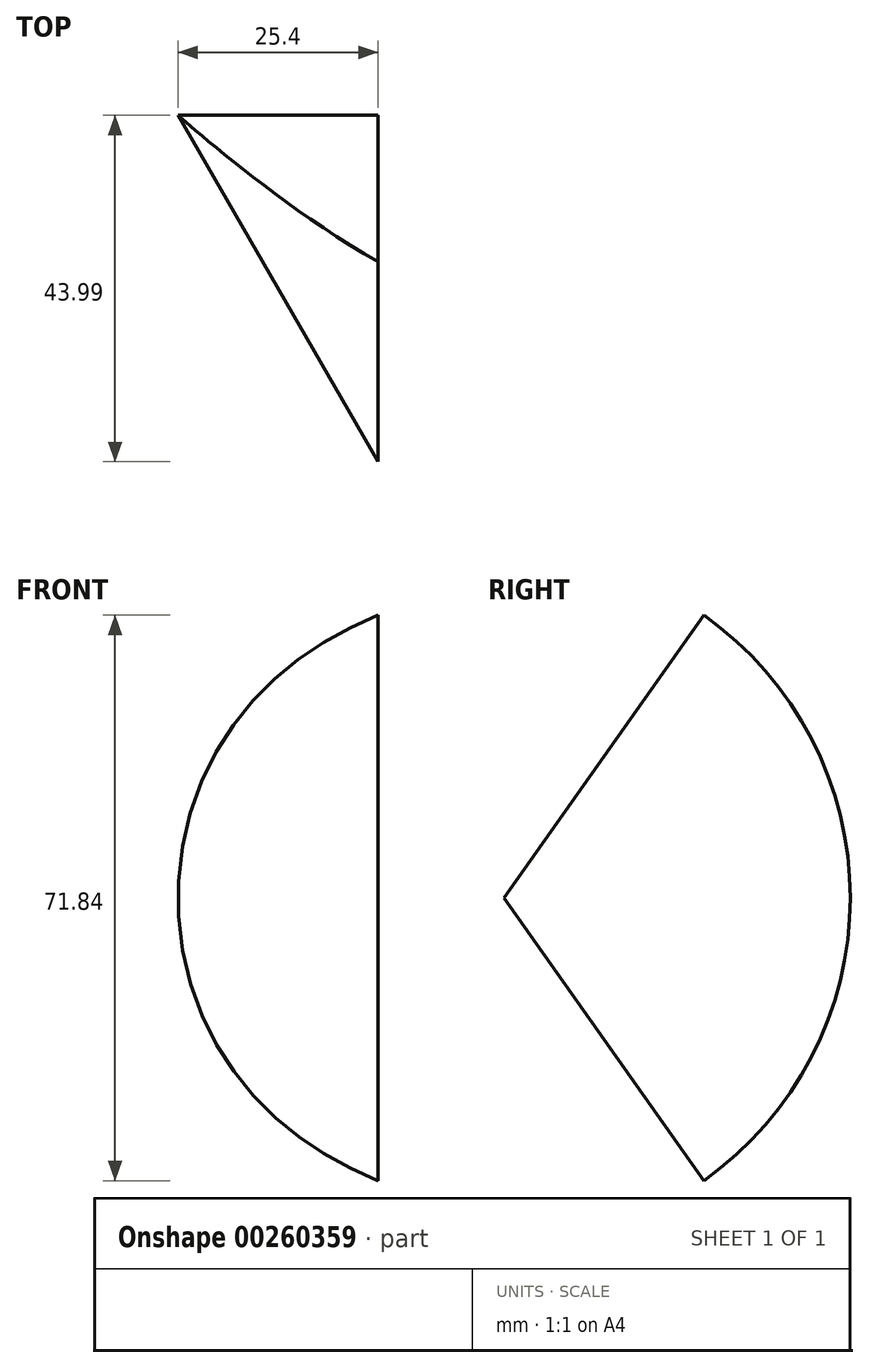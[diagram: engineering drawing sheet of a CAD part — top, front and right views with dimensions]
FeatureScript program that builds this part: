
annotation { "Feature Type Name" : "Feature", "Feature Type Description" : "" }
export const myFeature = defineFeature(function(context is Context, id is Id, definition is map)
    precondition{}
    {
        {
            var Q0;
            Q0=qCreatedBy(makeId("Top.planeOp"),FACE);
            var sketch = newSketch(context, id + "F0", { "sketchPlane" : qUnion([Q0])});
            skLineSegment(sketch, "E0", {"start": v(-25.4, 44) * mm, "end": v(25.4, 44) * mm});
            skLineSegment(sketch, "E1", {"start": v(25.4, 44) * mm, "end": v(50.8, 0) * mm});
            skLineSegment(sketch, "E2", {"start": v(50.8, 0) * mm, "end": v(25.4, -44) * mm});
            skLineSegment(sketch, "E3", {"start": v(25.4, -44) * mm, "end": v(-25.4, -44) * mm});
            skLineSegment(sketch, "E4", {"start": v(-25.4, -44) * mm, "end": v(-50.8, 0) * mm});
            skLineSegment(sketch, "E5", {"start": v(-50.8, 0) * mm, "end": v(-25.4, 44) * mm});
            skLineSegment(sketch, "E6", {"start": v(25.4, -44) * mm, "end": v(25.4, 0) * mm});
            skLineSegment(sketch, "E7", {"start": v(25.4, 0) * mm, "end": v(0, 0) * mm});
            skLineSegment(sketch, "E8", {"start": v(0, 0) * mm, "end": v(25.4, -44) * mm});
            skLineSegment(sketch, "E9", {"start": v(-25.4, -44) * mm, "end": v(0, 0) * mm});
            skLineSegment(sketch, "E10", {"start": v(25.4, 0) * mm, "end": v(50.8, 0) * mm});
            skSolve(sketch);
        }
        {
            var Q0;
            Q0=makeQuery(id+"F0.imprint","IMPRINT",FACE,{"disambiguationData":[TD([[makeQuery(id+"F0.imprint","IMPRINT",EDGE,{"derivedFrom":sQuery(id+"F0.wireOp",EDGE,"E6")}),1.0]])]});
            var Q1;
            Q1=makeQuery(id+"F0.imprint","IMPRINT",FACE,{"disambiguationData":[TD([[makeQuery(id+"F0.imprint","IMPRINT",EDGE,{"derivedFrom":sQuery(id+"F0.wireOp",EDGE,"E3")}),-1.0]])]});
            var Q2;
            Q2=sQuery(id+"F0.wireOp",EDGE,"E3");
            revolve(context, id + "F1", {"entities" : qUnion([Q0, Q1]), "axis" : qUnion([Q2]), "revolveType" : RevolveType.FULL});
        }
        {
            var Q0;
            Q0=makeQuery(id+"F0.imprint","IMPRINT",FACE,{"disambiguationData":[TD([[makeQuery(id+"F0.imprint","IMPRINT",EDGE,{"derivedFrom":sQuery(id+"F0.wireOp",EDGE,"E6")}),1.0]])]});
            var Q1;
            Q1=makeQuery(id+"F0.imprint","IMPRINT",FACE,{"disambiguationData":[TD([[makeQuery(id+"F0.imprint","IMPRINT",EDGE,{"derivedFrom":sQuery(id+"F0.wireOp",EDGE,"E2")}),-1.0]])]});
            var Q2;
            Q2=sQuery(id+"F0.wireOp",EDGE,"E2");
            revolve(context, id + "F2", {"entities" : qUnion([Q0, Q1]), "axis" : qUnion([Q2]), "revolveType" : RevolveType.FULL});
        }
        {
            var Q0;
            Q0=makeQuery(id+"F1.opRevolve","SWEPT_BODY",BODY,{"disambiguationData":[OSD([sQuery(id+"F0.wireOp",EDGE,"E3"),sQuery(id+"F0.wireOp",EDGE,"sWTZixaA-eX1T-PpJT-601t-vvLHwSXly7HI"),sQuery(id+"F0.wireOp",EDGE,"uKste7KS-KDV9-nmHI-dkTW-kthW4VJtHvLH"),sQuery(id+"F0.wireOp",EDGE,"VU5Et6aT-ZoFL-Rrf1-LmdR-srkngCvIAy6G")])]});
            var Q1;
            Q1=makeQuery(id+"F2.opRevolve","SWEPT_BODY",BODY,{"disambiguationData":[OSD([sQuery(id+"F0.wireOp",EDGE,"E2"),sQuery(id+"F0.wireOp",EDGE,"A6Zyu8FQ-YpJL-LcUI-DO5F-jcSyuetFniUV"),sQuery(id+"F0.wireOp",EDGE,"2pc9lHif-INIS-XHNU-3OGd-vn8x0dO5Td43")])]});
            booleanBodies(context, id + "F3", {"operationType" : BooleanOperationType.INTERSECTION, "tools" : qUnion([Q0, Q1])});
        }
        {
            var Q0;
            Q0=makeQuery(id+"F3.opBoolean","INTERSECT",VERTEX,{"disambiguationData":[OD(1.0)],"derivedFrom":[makeQuery(id+"F1.opRevolve","SWEPT_FACE",FACE,{"disambiguationData":[OSD([sQuery(id+"F0.wireOp",EDGE,"E6")])]}),makeQuery(id+"F1.opRevolve","SWEPT_FACE",FACE,{"disambiguationData":[OSD([sQuery(id+"F0.wireOp",EDGE,"E7")])]}),makeQuery(id+"F2.opRevolve","SWEPT_FACE",FACE,{"disambiguationData":[OSD([sQuery(id+"F0.wireOp",EDGE,"E8")])]})]});
            var Q1;
            Q1=sQuery(id+"F0.wireOp",VERTEX,"E2.end");
            var Q2;
            Q2=sQuery(id+"F0.wireOp",VERTEX,"E5.end");
            cPlane(context, id + "F4", {"entities" : qUnion([Q0, Q1, Q2]), "cplaneType" : CPlaneType.THREE_POINT, "offset" : 25.4 * mm, "width" : 152.4 * mm, "height" : 152.4 * mm});
        }
        {
            var Q0;
            Q0=qCreatedBy(id+"F4.planeOp",FACE);
            var sketch = newSketch(context, id + "F5", { "sketchPlane" : qUnion([Q0])});
            skLineSegment(sketch, "E11", {"start": v(-33.26, 38.4) * mm, "end": v(16.63, 48) * mm});
            skLineSegment(sketch, "E12", {"start": v(16.63, 48) * mm, "end": v(49.88, 9.6) * mm});
            skLineSegment(sketch, "E13", {"start": v(49.88, 9.6) * mm, "end": v(33.26, -38.4) * mm});
            skLineSegment(sketch, "E14", {"start": v(33.26, -38.4) * mm, "end": v(-16.63, -48) * mm});
            skLineSegment(sketch, "E15", {"start": v(-16.63, -48) * mm, "end": v(-49.88, -9.6) * mm});
            skLineSegment(sketch, "E16", {"start": v(-49.88, -9.6) * mm, "end": v(-33.26, 38.4) * mm});
            skSolve(sketch);
        }
        {
            var Q0;
            Q0=sQuery(id+"F5.wireOp",VERTEX,"E12.start");
            var Q1;
            Q1=sQuery(id+"F0.wireOp",VERTEX,"E2.start");
            var Q2;
            Q2=sQuery(id+"F0.wireOp",VERTEX,"E5.start");
            cPlane(context, id + "F6", {"entities" : qUnion([Q0, Q1, Q2]), "cplaneType" : CPlaneType.THREE_POINT, "offset" : 25.4 * mm, "width" : 152.4 * mm, "height" : 152.4 * mm});
        }
        {
            var Q0;
            Q0=qCreatedBy(id+"F6.planeOp",FACE);
            var sketch = newSketch(context, id + "F7", { "sketchPlane" : qUnion([Q0])});
            skLineSegment(sketch, "E17", {"start": v(50.8, 0) * mm, "end": v(25.4, 44) * mm});
            skLineSegment(sketch, "E18", {"start": v(25.4, 44) * mm, "end": v(-25.4, 44) * mm});
            skLineSegment(sketch, "E19", {"start": v(-25.4, 44) * mm, "end": v(-50.8, 0) * mm});
            skLineSegment(sketch, "E20", {"start": v(-50.8, 0) * mm, "end": v(-25.4, -44) * mm});
            skLineSegment(sketch, "E21", {"start": v(-25.4, -44) * mm, "end": v(25.4, -44) * mm});
            skLineSegment(sketch, "E22", {"start": v(25.4, -44) * mm, "end": v(50.8, 0) * mm});
            skSolve(sketch);
        }
        {
            var Q0;
            Q0=sQuery(id+"F5.wireOp",VERTEX,"E16.end");
            var Q1;
            Q1=sQuery(id+"F0.wireOp",VERTEX,"E4.start");
            var Q2;
            Q2=sQuery(id+"F0.wireOp",VERTEX,"E1.start");
            cPlane(context, id + "F8", {"entities" : qUnion([Q0, Q1, Q2]), "cplaneType" : CPlaneType.THREE_POINT, "offset" : 25.4 * mm, "width" : 152.4 * mm, "height" : 152.4 * mm});
        }
        {
            var Q0;
            Q0=qCreatedBy(id+"F8.planeOp",FACE);
            var sketch = newSketch(context, id + "F9", { "sketchPlane" : qUnion([Q0])});
            skLineSegment(sketch, "E23", {"start": v(-49.88, -9.6) * mm, "end": v(-33.26, 38.4) * mm});
            skLineSegment(sketch, "E24", {"start": v(-33.26, 38.4) * mm, "end": v(16.63, 48) * mm});
            skLineSegment(sketch, "E25", {"start": v(16.63, 48) * mm, "end": v(49.88, 9.6) * mm});
            skLineSegment(sketch, "E26", {"start": v(49.88, 9.6) * mm, "end": v(33.26, -38.4) * mm});
            skLineSegment(sketch, "E27", {"start": v(33.26, -38.4) * mm, "end": v(-16.63, -48) * mm});
            skLineSegment(sketch, "E28", {"start": v(-16.63, -48) * mm, "end": v(-49.88, -9.6) * mm});
            skSolve(sketch);
        }
        {
            var Q0;
            Q0=qCreatedBy(makeId("Top.planeOp"),FACE);
            var sketch = newSketch(context, id + "F10", { "sketchPlane" : qUnion([Q0])});
            skLineSegment(sketch, "E29", {"start": v(-25.4, -44) * mm, "end": v(50.8, 0) * mm});
            skLineSegment(sketch, "E30", {"start": v(50.8, 0) * mm, "end": v(-25.4, 44) * mm});
            skLineSegment(sketch, "E31", {"start": v(-25.4, 44) * mm, "end": v(-25.4, -44) * mm});
            skCircle(sketch, "E32", {"center": v(0, 0) * mm, "radius": 50.8 * mm});
            skSolve(sketch);
        }
        {
            var Q0;
            Q0=qCreatedBy(makeId("Top.planeOp"),FACE);
            var sketch = newSketch(context, id + "F11", { "sketchPlane" : qUnion([Q0])});
            skPoint(sketch, "E33", {"position": v(-25.4, 0) * mm});
            skPoint(sketch, "E34", {"position": v(12.7, 22) * mm});
            skPoint(sketch, "E35", {"position": v(12.7, -22) * mm});
            skLineSegment(sketch, "E36", {"start": v(-25.4, 0) * mm, "end": v(12.7, -22) * mm});
            skLineSegment(sketch, "E37", {"start": v(12.7, -22) * mm, "end": v(12.7, 22) * mm});
            skLineSegment(sketch, "E38", {"start": v(12.7, 22) * mm, "end": v(-25.4, 0) * mm});
            skSolve(sketch);
        }
    });
